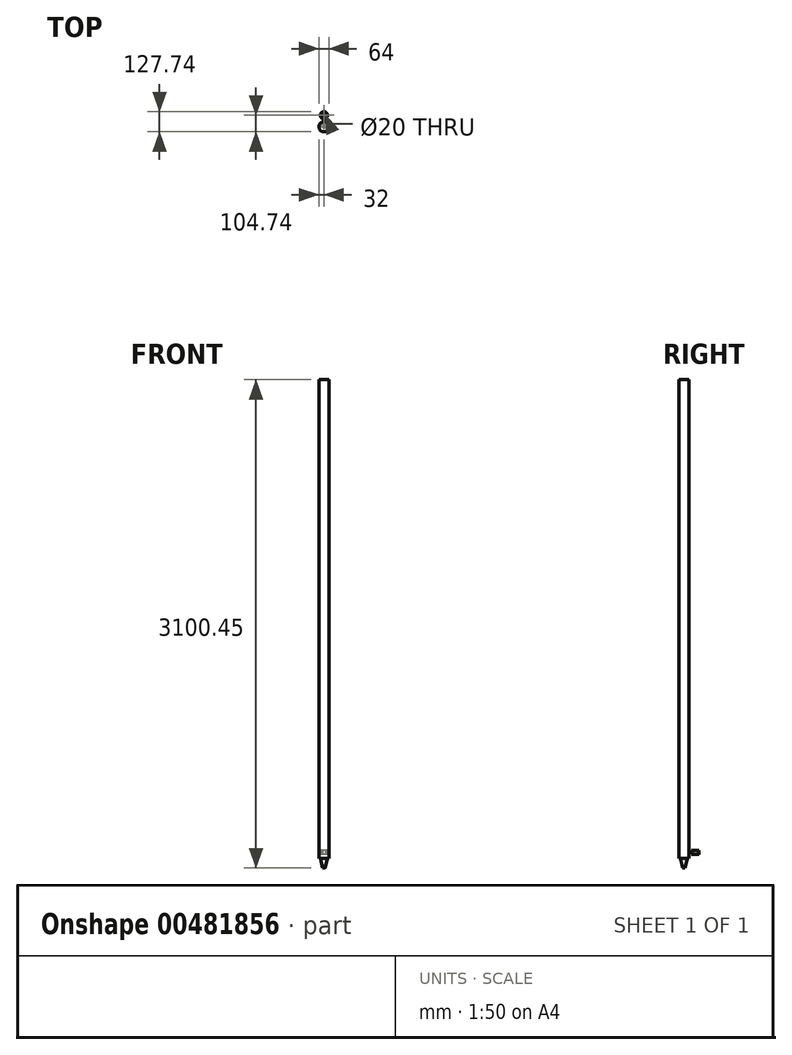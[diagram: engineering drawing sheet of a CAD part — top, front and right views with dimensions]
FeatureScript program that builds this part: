
annotation { "Feature Type Name" : "Feature", "Feature Type Description" : "" }
export const myFeature = defineFeature(function(context is Context, id is Id, definition is map)
    precondition{}
    {
        {
            var Q0;
            Q0=qCreatedBy(makeId("Top.planeOp"),FACE);
            var sketch = newSketch(context, id + "F0", { "sketchPlane" : qUnion([Q0])});
            skCircle(sketch, "E0", {"center": v(0, 0) * mm, "radius": 10 * mm});
            skCircle(sketch, "E1", {"center": v(0, 0) * mm, "radius": 23 * mm});
            skSolve(sketch);
        }
        {
            var Q0;
            Q0=makeQuery(id+"F0.imprint","IMPRINT",FACE,{"disambiguationData":[TD([[makeQuery(id+"F0.imprint","IMPRINT",EDGE,{"derivedFrom":sQuery(id+"F0.wireOp",EDGE,"E0")}),-1.0]])]});
            extrude(context, id + "F1", {"entities" : qUnion([Q0]), "depth" : 25 * mm});
        }
        {
            var Q0;
            Q0=qCreatedBy(makeId("Right.planeOp"),FACE);
            var sketch = newSketch(context, id + "F2", { "sketchPlane" : qUnion([Q0])});
            skLineSegment(sketch, "E2.bottom", {"start": v(-104.74, 3013.73) * mm, "end": v(-72.74, 3013.73) * mm});
            skLineSegment(sketch, "E2.top", {"start": v(-104.74, -26.27) * mm, "end": v(-94.36, -26.27) * mm});
            skLineSegment(sketch, "E2.left", {"start": v(-104.74, 3013.73) * mm, "end": v(-104.74, -26.27) * mm});
            skLineSegment(sketch, "E2.right", {"start": v(-72.74, 3013.73) * mm, "end": v(-72.74, -26.27) * mm});
            skLineSegment(sketch, "E3.left", {"start": v(-72.74, -26.27) * mm, "end": v(-72.74, -63.01) * mm});
            skLineSegment(sketch, "E4", {"start": v(-72.74, -63.01) * mm, "end": v(-72.74, -86.72) * mm});
            skLineSegment(sketch, "E5", {"start": v(-72.74, -86.72) * mm, "end": v(-80.24, -86.72) * mm});
            skPoint(sketch, "E6.end.orphan", {"position": v(-82.74, -63.01) * mm});
            skPoint(sketch, "E7.end.orphan", {"position": v(-81.5, -74.87) * mm});
            skLineSegment(sketch, "E8", {"start": v(-80.24, -86.72) * mm, "end": v(-94.36, -26.27) * mm});
            skLineSegment(sketch, "E9.trimOffspring", {"start": v(-82.74, -26.27) * mm, "end": v(-72.74, -26.27) * mm});
            skSolve(sketch);
        }
        {
            var Q0;
            Q0=makeQuery(id+"F2.imprint","IMPRINT",FACE,{"disambiguationData":[TD([[makeQuery(id+"F2.imprint","IMPRINT",EDGE,{"derivedFrom":sQuery(id+"F2.wireOp",EDGE,"E3.bottom")}),1.0]])]});
            var Q1;
            Q1=makeQuery(id+"F2.imprint","IMPRINT",FACE,{"disambiguationData":[TD([[makeQuery(id+"F2.imprint","IMPRINT",EDGE,{"derivedFrom":sQuery(id+"F2.wireOp",EDGE,"E3.top")}),1.0]])]});
            var Q2;
            Q2=makeQuery(id+"F2.imprint","IMPRINT",FACE,{"disambiguationData":[TD([[makeQuery(id+"F2.imprint","IMPRINT",EDGE,{"derivedFrom":sQuery(id+"F2.wireOp",EDGE,"E2.bottom")}),-1.0]])]});
            var Q3;
            Q3=sQuery(id+"F2.wireOp",EDGE,"E2.right");
            revolve(context, id + "F3", {"entities" : qUnion([Q0, Q1, Q2]), "axis" : qUnion([Q3]), "revolveType" : RevolveType.FULL});
        }
    });
